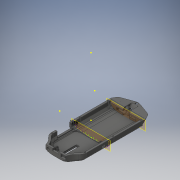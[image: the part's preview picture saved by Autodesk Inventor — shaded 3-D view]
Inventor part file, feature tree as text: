
AUTODESK INVENTOR PART (.ipt)
format: ipt  version: 2016 (Build 200138000, 138)  size: 26,497,536 bytes
history: native  units: in
note: dims shown in document units (in); Inventor stores cm internally (conversion verified against a paired STEP export)
features: other x3, plane x2, sketch x2, projected_geometry x1
ambient origin geometry x8: Origin, YZ Plane, XZ Plane, XY Plane, X Axis, Y Axis, Z Axis, Center Point
bodies: Solid1 (feature_tree)
feature tree (8):
  other  "ehlers_enclosure.ipt"
  plane  "Work Plane3"
  sketch  "Sketch1"  dims[d0=0.3937in]
  sketch  "Sketch2"  dims[d2=0.1378in]
  other  "print::ehlers_enclosure.ipt"
  other  "TaggingFeature1"
  plane  "Work Plane2"
  projected_geometry  "Project Cut Edges1"
